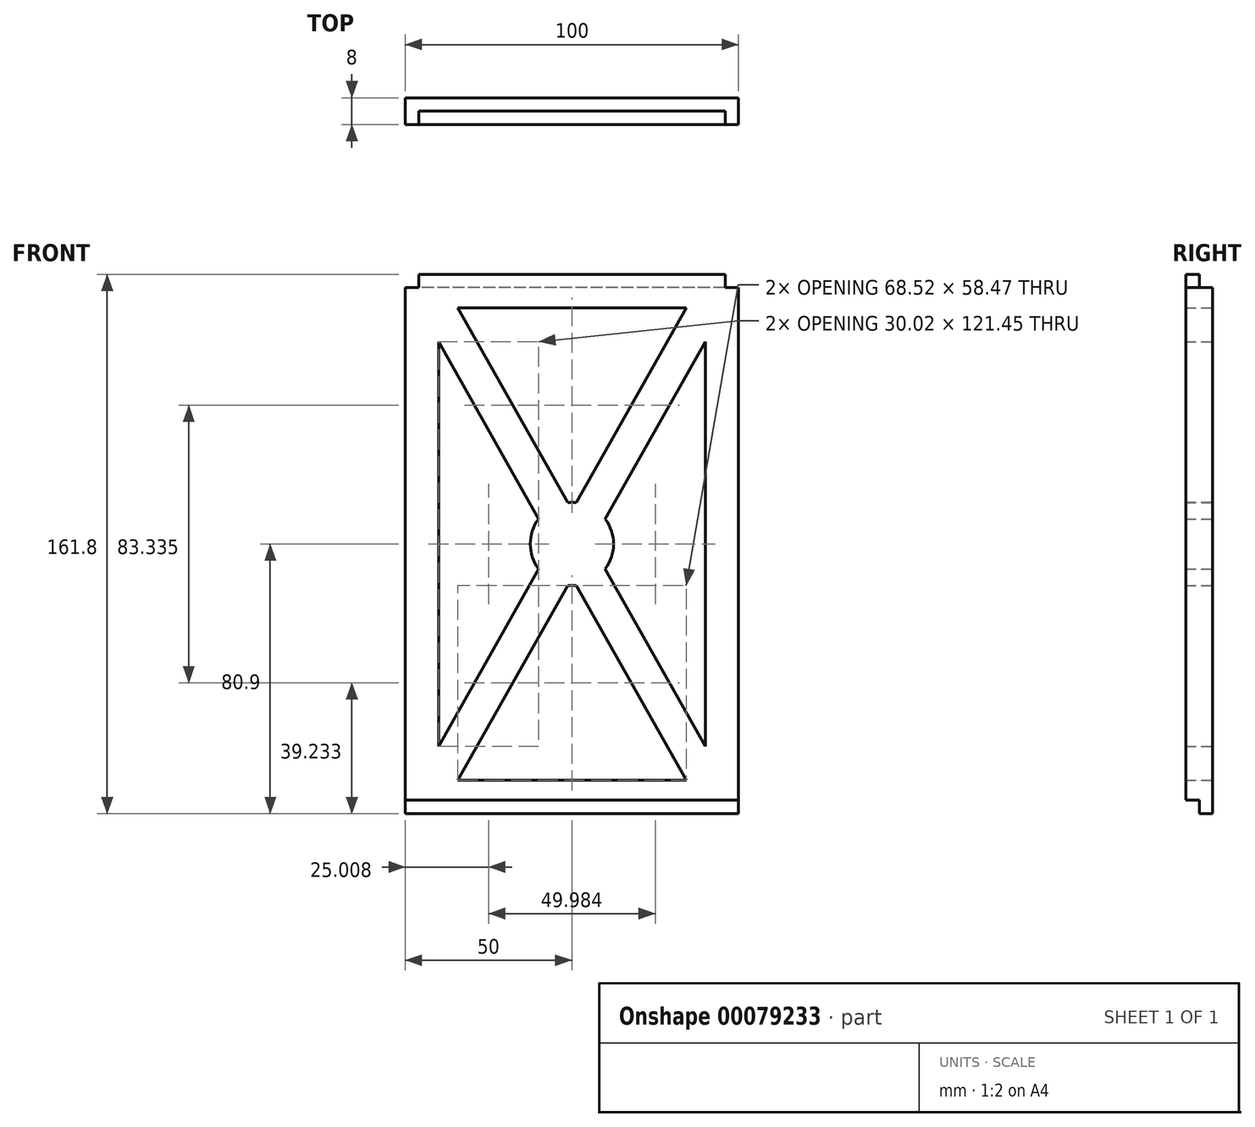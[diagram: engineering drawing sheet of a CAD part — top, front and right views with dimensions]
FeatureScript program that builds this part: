
annotation { "Feature Type Name" : "Feature", "Feature Type Description" : "" }
export const myFeature = defineFeature(function(context is Context, id is Id, definition is map)
    precondition{}
    {
        {
            var Q0;
            Q0=qCreatedBy(makeId("Front.planeOp"),FACE);
            var sketch = newSketch(context, id + "F0", { "sketchPlane" : qUnion([Q0])});
            skLineSegment(sketch, "E0.left", {"start": v(0, 0) * mm, "end": v(0, 0) * mm});
            skLineSegment(sketch, "E0.right", {"start": v(8.2, 0) * mm, "end": v(8.2, 0) * mm});
            skLineSegment(sketch, "E1.top", {"start": v(100, 161.8) * mm, "end": v(0, 161.8) * mm});
            skLineSegment(sketch, "E1.left", {"start": v(100, 0) * mm, "end": v(100, 161.8) * mm});
            skLineSegment(sketch, "E1.right", {"start": v(0, 0) * mm, "end": v(0, 161.8) * mm});
            skLineSegment(sketch, "E2", {"start": v(0, 0) * mm, "end": v(100, 0) * mm});
            skLineSegment(sketch, "E3.0", {"start": v(10, 20.18) * mm, "end": v(10, 141.62) * mm});
            skLineSegment(sketch, "E3.1", {"start": v(15.74, 10) * mm, "end": v(84.26, 10) * mm});
            skLineSegment(sketch, "E3.2", {"start": v(90, 20.18) * mm, "end": v(90, 141.62) * mm});
            skLineSegment(sketch, "E3.3", {"start": v(84.26, 151.8) * mm, "end": v(15.74, 151.8) * mm});
            skLineSegment(sketch, "E4", {"start": v(100, 80.9) * mm, "end": v(0, 80.9) * mm, "construction": true});
            skLineSegment(sketch, "E5", {"start": v(50, 161.8) * mm, "end": v(50, 0) * mm, "construction": true});
            skArc(sketch, "E6", {"start": v(48.73, 68.47) * mm, "mid": v(50, 68.4) * mm, "end": v(51.27, 68.47) * mm});
            skLineSegment(sketch, "E7.0", {"start": v(15.74, 10) * mm, "end": v(48.73, 68.47) * mm});
            skLineSegment(sketch, "E8.0", {"start": v(10, 20.18) * mm, "end": v(40.02, 73.38) * mm});
            skLineSegment(sketch, "E9.MirrorCS", {"start": v(84.26, 10) * mm, "end": v(51.27, 68.47) * mm});
            skLineSegment(sketch, "E10.MirrorCS", {"start": v(90, 20.18) * mm, "end": v(59.98, 73.38) * mm});
            skLineSegment(sketch, "E11.MirrorCS", {"start": v(10, 141.62) * mm, "end": v(40.02, 88.42) * mm});
            skLineSegment(sketch, "E12.MirrorCS", {"start": v(15.74, 151.8) * mm, "end": v(48.73, 93.33) * mm});
            skLineSegment(sketch, "E13.MirrorCS", {"start": v(84.26, 151.8) * mm, "end": v(51.27, 93.33) * mm});
            skLineSegment(sketch, "E14.MirrorCS", {"start": v(90, 141.62) * mm, "end": v(59.98, 88.42) * mm});
            skArc(sketch, "E15.trimOffspring", {"start": v(59.98, 73.38) * mm, "mid": v(62.5, 80.9) * mm, "end": v(59.98, 88.42) * mm});
            skArc(sketch, "E16.trimOffspring", {"start": v(51.27, 93.33) * mm, "mid": v(50, 93.4) * mm, "end": v(48.73, 93.33) * mm});
            skArc(sketch, "E17.trimOffspring", {"start": v(40.02, 88.42) * mm, "mid": v(37.5, 80.9) * mm, "end": v(40.02, 73.38) * mm});
            skSolve(sketch);
        }
        {
            var Q0;
            Q0=makeQuery(id+"F0.imprint","IMPRINT",FACE,{"disambiguationData":[TD([[makeQuery(id+"F0.imprint","IMPRINT",EDGE,{"derivedFrom":sQuery(id+"F0.wireOp",EDGE,"E1.top")}),1.0]])]});
            extrude(context, id + "F1", {"entities" : qUnion([Q0]), "depth" : 8 * mm});
        }
        {
            var Q0;
            Q0=makeQuery(id+"F1.opExtrude","SWEPT_FACE",FACE,{"disambiguationData":[OSD([sQuery(id+"F0.wireOp",EDGE,"E1.right")])]});
            var sketch = newSketch(context, id + "F2", { "sketchPlane" : qUnion([Q0])});
            skPoint(sketch, "E18.oppositeSnap0", {"position": v(4, 0) * mm});
            skLineSegment(sketch, "E18.bottom", {"start": v(8, 0) * mm, "end": v(4, 0) * mm});
            skLineSegment(sketch, "E18.top", {"start": v(8, 4) * mm, "end": v(4, 4) * mm});
            skLineSegment(sketch, "E18.left", {"start": v(8, 0) * mm, "end": v(8, 4) * mm});
            skLineSegment(sketch, "E18.right", {"start": v(4, 0) * mm, "end": v(4, 4) * mm});
            skLineSegment(sketch, "E19", {"start": v(4, 161.8) * mm, "end": v(4, 0) * mm, "construction": true});
            skLineSegment(sketch, "E20", {"start": v(4, 80.9) * mm, "end": v(22.47, 80.9) * mm, "construction": true});
            skPoint(sketch, "E20.endSnap0", {"position": v(4, 80.9) * mm});
            skLineSegment(sketch, "E21.MirrorCS", {"start": v(4, 161.8) * mm, "end": v(4, 157.8) * mm});
            skLineSegment(sketch, "E22.MirrorCS", {"start": v(0, 161.8) * mm, "end": v(4, 161.8) * mm});
            skLineSegment(sketch, "E23.MirrorCS", {"start": v(0, 157.8) * mm, "end": v(4, 157.8) * mm});
            skLineSegment(sketch, "E24.MirrorCS", {"start": v(0, 161.8) * mm, "end": v(0, 157.8) * mm});
            skPoint(sketch, "E25.MirrorCS.end.orphan", {"position": v(4, 161.8) * mm});
            skPoint(sketch, "E25.MirrorCS.start.orphan", {"position": v(8, 161.8) * mm});
            skPoint(sketch, "E26.MirrorCS.end.orphan", {"position": v(8, 157.8) * mm});
            skPoint(sketch, "E27.MirrorCS.end.orphan", {"position": v(4, 157.8) * mm});
            skSolve(sketch);
        }
        {
            var Q0;
            Q0=makeQuery(id+"F2.imprint","IMPRINT",FACE,{"disambiguationData":[TD([[makeQuery(id+"F2.imprint","IMPRINT",EDGE,{"derivedFrom":sQuery(id+"F2.wireOp",EDGE,"E22.MirrorCS")}),1.0]])]});
            var Q1;
            Q1=makeQuery(id+"F2.imprint","IMPRINT",FACE,{"disambiguationData":[TD([[makeQuery(id+"F2.imprint","IMPRINT",EDGE,{"derivedFrom":sQuery(id+"F2.wireOp",EDGE,"E18.bottom")}),-1.0]])]});
            extrude(context, id + "F3", {"entities" : qUnion([Q0, Q1]), "operationType" : NewBodyOperationType.REMOVE, "oppositeDirection" : true, "depth" : 134.45 * mm});
        }
        {
            var Q0;
            Q0=makeQuery(id+"F1.opExtrude","SWEPT_FACE",FACE,{"disambiguationData":[OSD([sQuery(id+"F0.wireOp",EDGE,"E1.top")])]});
            var sketch = newSketch(context, id + "F4", { "sketchPlane" : qUnion([Q0])});
            skLineSegment(sketch, "E28", {"start": v(50, -8) * mm, "end": v(50, 45.33) * mm, "construction": true});
            skPoint(sketch, "E28.endSnap0", {"position": v(50, -4) * mm});
            skLineSegment(sketch, "E29.bottom", {"start": v(100, -8) * mm, "end": v(96, -8) * mm});
            skLineSegment(sketch, "E29.top", {"start": v(100, -4) * mm, "end": v(96, -4) * mm});
            skLineSegment(sketch, "E29.left", {"start": v(100, -8) * mm, "end": v(100, -4) * mm});
            skLineSegment(sketch, "E29.right", {"start": v(96, -8) * mm, "end": v(96, -4) * mm});
            skLineSegment(sketch, "E30.MirrorCS", {"start": v(0, -8) * mm, "end": v(0, -4) * mm});
            skLineSegment(sketch, "E31.MirrorCS", {"start": v(0, -8) * mm, "end": v(4, -8) * mm});
            skLineSegment(sketch, "E32.MirrorCS", {"start": v(0, -4) * mm, "end": v(4, -4) * mm});
            skLineSegment(sketch, "E33.MirrorCS", {"start": v(4, -8) * mm, "end": v(4, -4) * mm});
            skSolve(sketch);
        }
        {
            var Q0;
            Q0=makeQuery(id+"F4.imprint","IMPRINT",FACE,{"disambiguationData":[TD([[makeQuery(id+"F4.imprint","IMPRINT",EDGE,{"derivedFrom":sQuery(id+"F4.wireOp",EDGE,"E29.bottom")}),-1.0]])]});
            var Q1;
            Q1=makeQuery(id+"F4.imprint","IMPRINT",FACE,{"disambiguationData":[TD([[makeQuery(id+"F4.imprint","IMPRINT",EDGE,{"derivedFrom":sQuery(id+"F4.wireOp",EDGE,"E30.MirrorCS")}),-1.0]])]});
            extrude(context, id + "F5", {"entities" : qUnion([Q0, Q1]), "operationType" : NewBodyOperationType.REMOVE, "oppositeDirection" : true, "depth" : 4 * mm});
        }
    });
